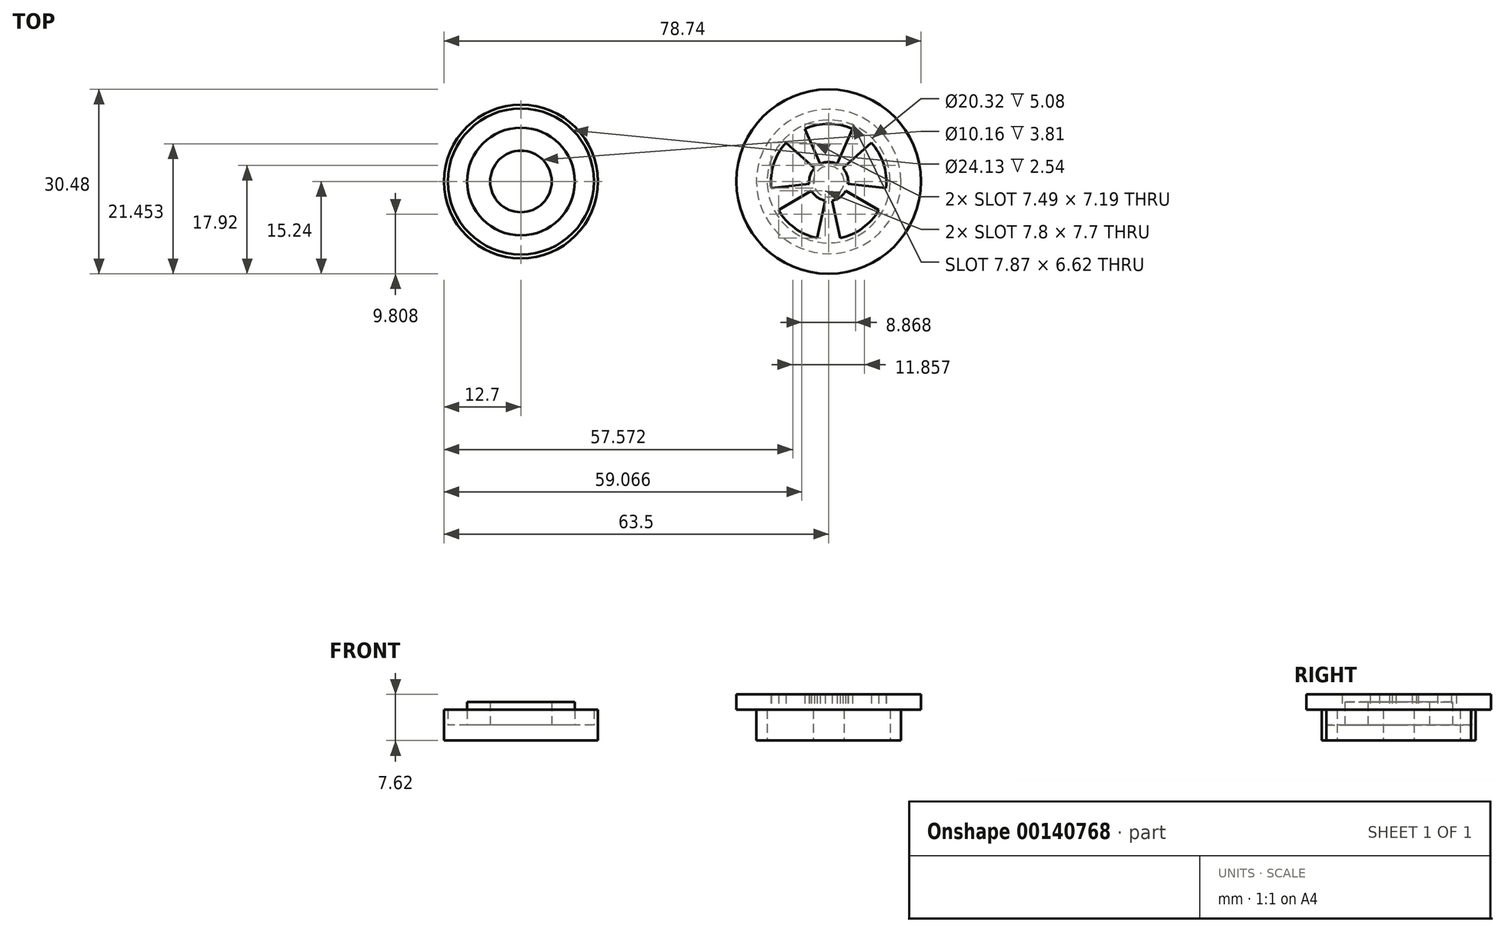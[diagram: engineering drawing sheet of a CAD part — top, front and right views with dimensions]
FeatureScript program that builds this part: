
annotation { "Feature Type Name" : "Feature", "Feature Type Description" : "" }
export const myFeature = defineFeature(function(context is Context, id is Id, definition is map)
    precondition{}
    {
        {
            var Q0;
            Q0=qCreatedBy(makeId("Top.planeOp"),FACE);
            var sketch = newSketch(context, id + "F0", { "sketchPlane" : qUnion([Q0])});
            skCircle(sketch, "E0", {"center": v(0, 0) * mm, "radius": 5.72 * mm});
            skCircle(sketch, "E1", {"center": v(0, 0) * mm, "radius": 12.7 * mm});
            skSolve(sketch);
        }
        {
            var Q0;
            Q0 = qSketchRegion(id + "F0", true);
            var Q1;
            Q1=makeQuery(id+"F0.imprint","IMPRINT",FACE,{"disambiguationData":[TD([[makeQuery(id+"F0.imprint","IMPRINT",EDGE,{"derivedFrom":sQuery(id+"F0.wireOp",EDGE,"E0")}),1.0]])]});
            extrude(context, id + "F1", {"entities" : qUnion([Q0, Q1]), "depth" : 2.54 * mm});
        }
        {
            var Q0;
            Q0=makeQuery(id+"F1.opExtrude","CAP_FACE",FACE,{"disambiguationData":[OSD([sQuery(id+"F0.wireOp",EDGE,"E1")])],"isStart":false});
            var sketch = newSketch(context, id + "F2", { "sketchPlane" : qUnion([Q0])});
            skCircle(sketch, "E2", {"center": v(0, 0) * mm, "radius": 5.08 * mm});
            skCircle(sketch, "E3", {"center": v(0, 0) * mm, "radius": 8.9 * mm});
            skSolve(sketch);
        }
        {
            var Q0;
            Q0 = qSketchRegion(id + "F2", true);
            extrude(context, id + "F3", {"entities" : qUnion([Q0]), "operationType" : NewBodyOperationType.ADD, "depth" : 3.8 * mm});
        }
        {
            var Q0;
            {var subQ0=sQuery(id+"F0.wireOp",EDGE,"E1");Q0=makeQuery(id+"F3.boolean.opBoolean","SPLIT",FACE,{"disambiguationData":[TD([makeQuery(id+"F1.opExtrude","SWEPT_FACE",FACE,{"disambiguationData":[OSD([subQ0])]})])],"derivedFrom":makeQuery(id+"F1.opExtrude","CAP_FACE",FACE,{"disambiguationData":[OSD([subQ0])],"isStart":false})});}
            var sketch = newSketch(context, id + "F4", { "sketchPlane" : qUnion([Q0])});
            skCircle(sketch, "E4", {"center": v(0, 0) * mm, "radius": 12.07 * mm});
            skCircle(sketch, "E5.0", {"center": v(0, 0) * mm, "radius": 12.7 * mm});
            skSolve(sketch);
        }
        {
            var Q0;
            Q0 = qSketchRegion(id + "F4", true);
            extrude(context, id + "F5", {"entities" : qUnion([Q0]), "operationType" : NewBodyOperationType.ADD, "depth" : 2.54 * mm});
        }
        {
            var Q0;
            Q0=qCreatedBy(makeId("Top.planeOp"),FACE);
            var sketch = newSketch(context, id + "F6", { "sketchPlane" : qUnion([Q0])});
            skCircle(sketch, "E6", {"center": v(50.8, 0) * mm, "radius": 2.54 * mm});
            skCircle(sketch, "E7", {"center": v(50.8, 0) * mm, "radius": 10.16 * mm});
            skCircle(sketch, "E8", {"center": v(50.8, 0) * mm, "radius": 11.94 * mm});
            skSolve(sketch);
        }
        {
            var Q0;
            Q0 = qSketchRegion(id + "F6", true);
            var Q1;
            Q1=makeQuery(id+"F6.imprint","IMPRINT",FACE,{"disambiguationData":[TD([[makeQuery(id+"F6.imprint","IMPRINT",EDGE,{"derivedFrom":sQuery(id+"F6.wireOp",EDGE,"E6")}),1.0]])]});
            extrude(context, id + "F7", {"entities" : qUnion([Q0, Q1]), "depth" : 5.08 * mm});
        }
        {
            var Q0;
            Q0=makeQuery(id+"F7.opExtrude","CAP_FACE",FACE,{"disambiguationData":[OSD([sQuery(id+"F6.wireOp",EDGE,"E7"),sQuery(id+"F6.wireOp",EDGE,"E8")])],"isStart":false});
            var sketch = newSketch(context, id + "F8", { "sketchPlane" : qUnion([Q0])});
            skCircle(sketch, "E9", {"center": v(50.8, 0) * mm, "radius": 15.24 * mm});
            skSolve(sketch);
        }
        {
            var Q0;
            Q0 = qSketchRegion(id + "F8", true);
            extrude(context, id + "F9", {"entities" : qUnion([Q0]), "depth" : 2.54 * mm});
        }
        {
            var Q0;
            Q0=makeQuery(id+"F9.opExtrude","SWEPT_BODY",BODY,{"disambiguationData":[OSD([sQuery(id+"F8.wireOp",EDGE,"E9")])]});
            var Q1;
            Q1=makeQuery(id+"F7.opExtrude","SWEPT_BODY",BODY,{"disambiguationData":[OSD([sQuery(id+"F6.wireOp",EDGE,"E7"),sQuery(id+"F6.wireOp",EDGE,"E8")])]});
            var Q2;
            Q2=makeQuery(id+"F7.opExtrude","SWEPT_BODY",BODY,{"disambiguationData":[OSD([sQuery(id+"F6.wireOp",EDGE,"E6")])]});
            booleanBodies(context, id + "F10", {"operationType" : BooleanOperationType.UNION, "tools" : qUnion([Q0, Q1, Q2])});
        }
        {
            var Q0;
            Q0=makeQuery(id+"F10.opBoolean","SPLIT",FACE,{"disambiguationData":[TD([makeQuery(id+"F7.opExtrude","SWEPT_FACE",FACE,{"disambiguationData":[OSD([sQuery(id+"F6.wireOp",EDGE,"E6")])]})])],"derivedFrom":makeQuery(id+"F9.opExtrude","CAP_FACE",FACE,{"disambiguationData":[OSD([sQuery(id+"F8.wireOp",EDGE,"E9")])],"isStart":true})});
            var sketch = newSketch(context, id + "F11", { "sketchPlane" : qUnion([Q0])});
            skArc(sketch, "E10", {"start": v(49.42, -2.9) * mm, "mid": v(50.8, -3.21) * mm, "end": v(52.18, -2.9) * mm});
            skLineSegment(sketch, "E11", {"start": v(50.8, 0) * mm, "end": v(50.8, -18.06) * mm});
            skArc(sketch, "E12", {"start": v(46.86, -8.67) * mm, "mid": v(50.8, -9.53) * mm, "end": v(54.74, -8.67) * mm});
            skLineSegment(sketch, "E13", {"start": v(49.42, -2.9) * mm, "end": v(46.86, -8.67) * mm});
            skLineSegment(sketch, "E14.MirrorCS", {"start": v(52.18, -2.9) * mm, "end": v(54.74, -8.67) * mm});
            skLineSegment(sketch, "E15.1.0", {"start": v(53.99, 0.42) * mm, "end": v(60.27, 1.06) * mm});
            skArc(sketch, "E15.1.1", {"start": v(53.13, -2.21) * mm, "mid": v(53.86, -1) * mm, "end": v(53.99, 0.42) * mm});
            skLineSegment(sketch, "E15.1.2", {"start": v(53.13, -2.21) * mm, "end": v(57.83, -6.42) * mm});
            skArc(sketch, "E15.1.3", {"start": v(57.83, -6.42) * mm, "mid": v(59.86, -2.94) * mm, "end": v(60.27, 1.06) * mm});
            skLineSegment(sketch, "E15.2.0", {"start": v(51.39, 3.16) * mm, "end": v(52.71, 9.33) * mm});
            skArc(sketch, "E15.2.1", {"start": v(53.63, 1.53) * mm, "mid": v(52.69, 2.6) * mm, "end": v(51.39, 3.16) * mm});
            skLineSegment(sketch, "E15.2.2", {"start": v(53.63, 1.53) * mm, "end": v(59.08, 4.7) * mm});
            skArc(sketch, "E15.2.3", {"start": v(59.08, 4.7) * mm, "mid": v(56.4, 7.7) * mm, "end": v(52.71, 9.33) * mm});
            skLineSegment(sketch, "E15.3.0", {"start": v(47.97, 1.53) * mm, "end": v(42.52, 4.7) * mm});
            skArc(sketch, "E15.3.1", {"start": v(50.21, 3.16) * mm, "mid": v(48.91, 2.6) * mm, "end": v(47.97, 1.53) * mm});
            skLineSegment(sketch, "E15.3.2", {"start": v(50.21, 3.16) * mm, "end": v(48.89, 9.33) * mm});
            skArc(sketch, "E15.3.3", {"start": v(48.89, 9.33) * mm, "mid": v(45.2, 7.7) * mm, "end": v(42.52, 4.7) * mm});
            skLineSegment(sketch, "E15.4.0", {"start": v(48.47, -2.21) * mm, "end": v(43.77, -6.42) * mm});
            skArc(sketch, "E15.4.1", {"start": v(47.61, 0.42) * mm, "mid": v(47.74, -1) * mm, "end": v(48.47, -2.21) * mm});
            skLineSegment(sketch, "E15.4.2", {"start": v(47.61, 0.42) * mm, "end": v(41.33, 1.06) * mm});
            skArc(sketch, "E15.4.3", {"start": v(41.33, 1.06) * mm, "mid": v(41.74, -2.94) * mm, "end": v(43.77, -6.42) * mm});
            skSolve(sketch);
        }
        {
            var Q0;
            Q0 = qSketchRegion(id + "F11", true);
            extrude(context, id + "F12", {"entities" : qUnion([Q0]), "operationType" : NewBodyOperationType.REMOVE, "oppositeDirection" : true, "depth" : 25.4 * mm});
        }
    });
